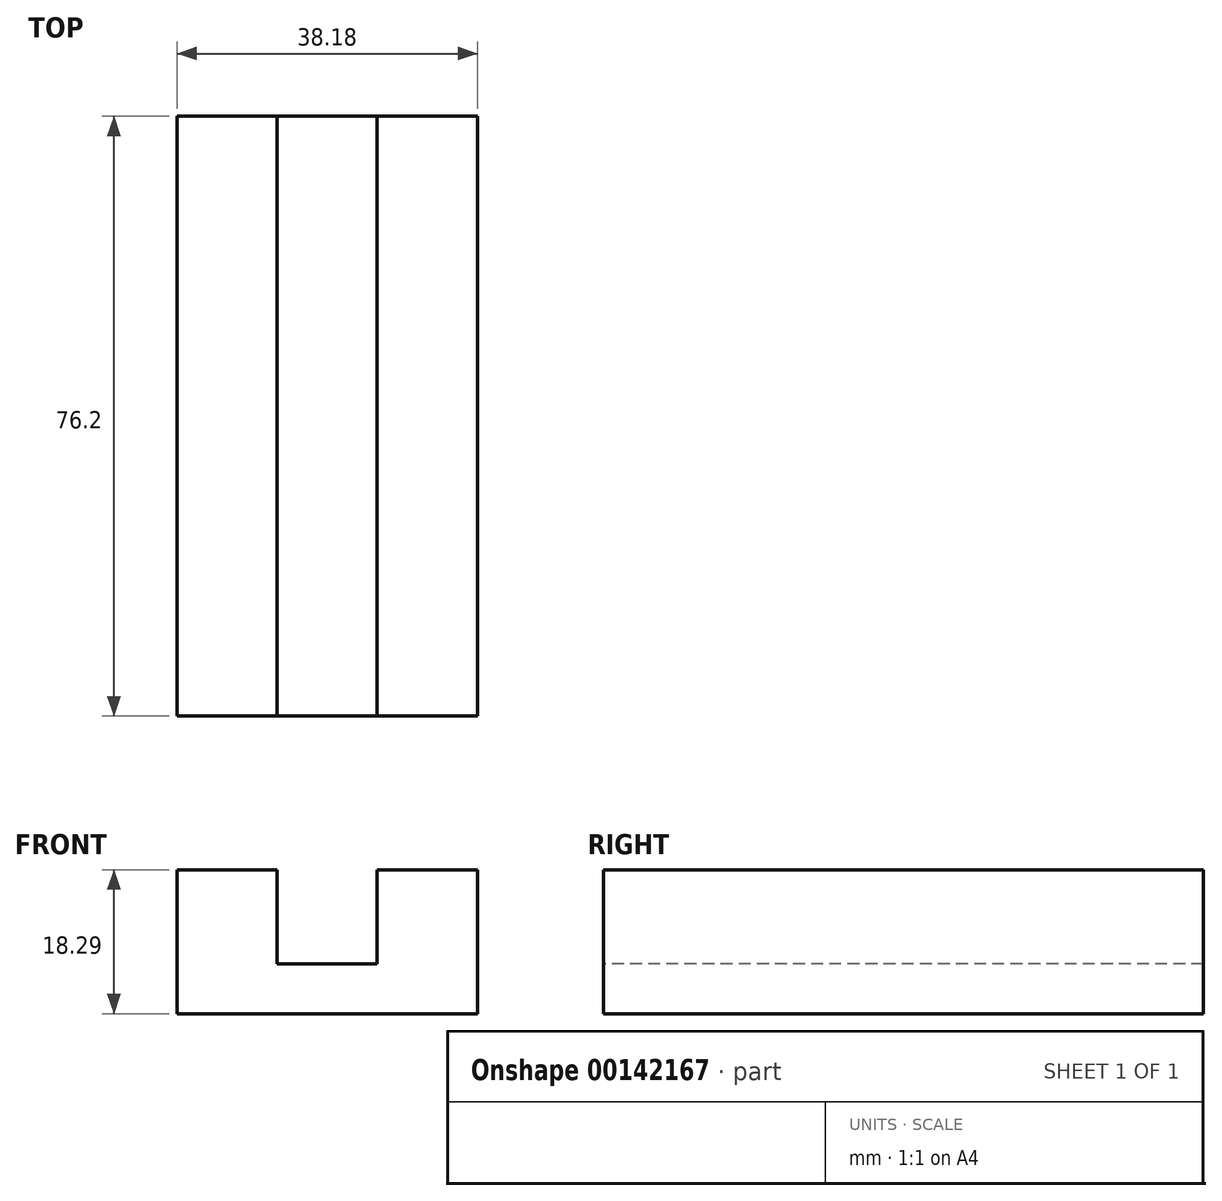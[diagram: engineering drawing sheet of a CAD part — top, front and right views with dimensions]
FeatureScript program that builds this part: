
annotation { "Feature Type Name" : "Feature", "Feature Type Description" : "" }
export const myFeature = defineFeature(function(context is Context, id is Id, definition is map)
    precondition{}
    {
        {
            var Q0;
            Q0=qCreatedBy(makeId("Top.planeOp"),FACE);
            var sketch = newSketch(context, id + "F0", { "sketchPlane" : qUnion([Q0])});
            skLineSegment(sketch, "E0.bottom", {"start": v(19.09, 38.1) * mm, "end": v(-19.09, 38.1) * mm});
            skLineSegment(sketch, "E0.top", {"start": v(19.09, -38.1) * mm, "end": v(-19.09, -38.1) * mm});
            skLineSegment(sketch, "E0.left", {"start": v(19.09, 38.1) * mm, "end": v(19.09, -38.1) * mm});
            skLineSegment(sketch, "E0.right", {"start": v(-19.09, 38.1) * mm, "end": v(-19.09, -38.1) * mm});
            skPoint(sketch, "E0.middle", {"position": v(0, 0) * mm});
            skSolve(sketch);
        }
        {
            var Q0;
            Q0 = qSketchRegion(id + "F0", true);
            extrude(context, id + "F1", {"entities" : qUnion([Q0]), "oppositeDirection" : true, "depth" : 6.35 * mm});
        }
        {
            var Q0;
            Q0=makeQuery(id+"F1.opExtrude","CAP_FACE",FACE,{"disambiguationData":[OSD([sQuery(id+"F0.wireOp",EDGE,"E0.bottom"),sQuery(id+"F0.wireOp",EDGE,"E0.top"),sQuery(id+"F0.wireOp",EDGE,"E0.left"),sQuery(id+"F0.wireOp",EDGE,"E0.right")])],"isStart":true});
            var sketch = newSketch(context, id + "F2", { "sketchPlane" : qUnion([Q0])});
            skLineSegment(sketch, "E1", {"start": v(-6.36, 38.1) * mm, "end": v(-6.36, -38.1) * mm});
            skPoint(sketch, "E1.endSnap0", {"position": v(0, -38.1) * mm});
            skLineSegment(sketch, "E2", {"start": v(6.36, 38.1) * mm, "end": v(6.36, -38.1) * mm});
            skSolve(sketch);
        }
        {
            var Q0;
            {var subQ0=sQuery(id+"F2.wireOp",EDGE,"E1");Q0=makeQuery(id+"F2.imprint","IMPRINT",FACE,{"disambiguationData":[TD([[makeQuery(id+"F2.imprint","IMPRINT",EDGE,{"derivedFrom":subQ0}),-1.0]])]});}
            extrude(context, id + "F3", {"entities" : qUnion([Q0]), "operationType" : NewBodyOperationType.ADD, "depth" : 11.94 * mm});
        }
        {
            var Q0;
            {var subQ0=sQuery(id+"F2.wireOp",EDGE,"E2");Q0=makeQuery(id+"F2.imprint","IMPRINT",FACE,{"disambiguationData":[TD([[makeQuery(id+"F2.imprint","IMPRINT",EDGE,{"derivedFrom":subQ0}),1.0]])]});}
            extrude(context, id + "F4", {"entities" : qUnion([Q0]), "operationType" : NewBodyOperationType.ADD, "depth" : 11.94 * mm});
        }
    });
